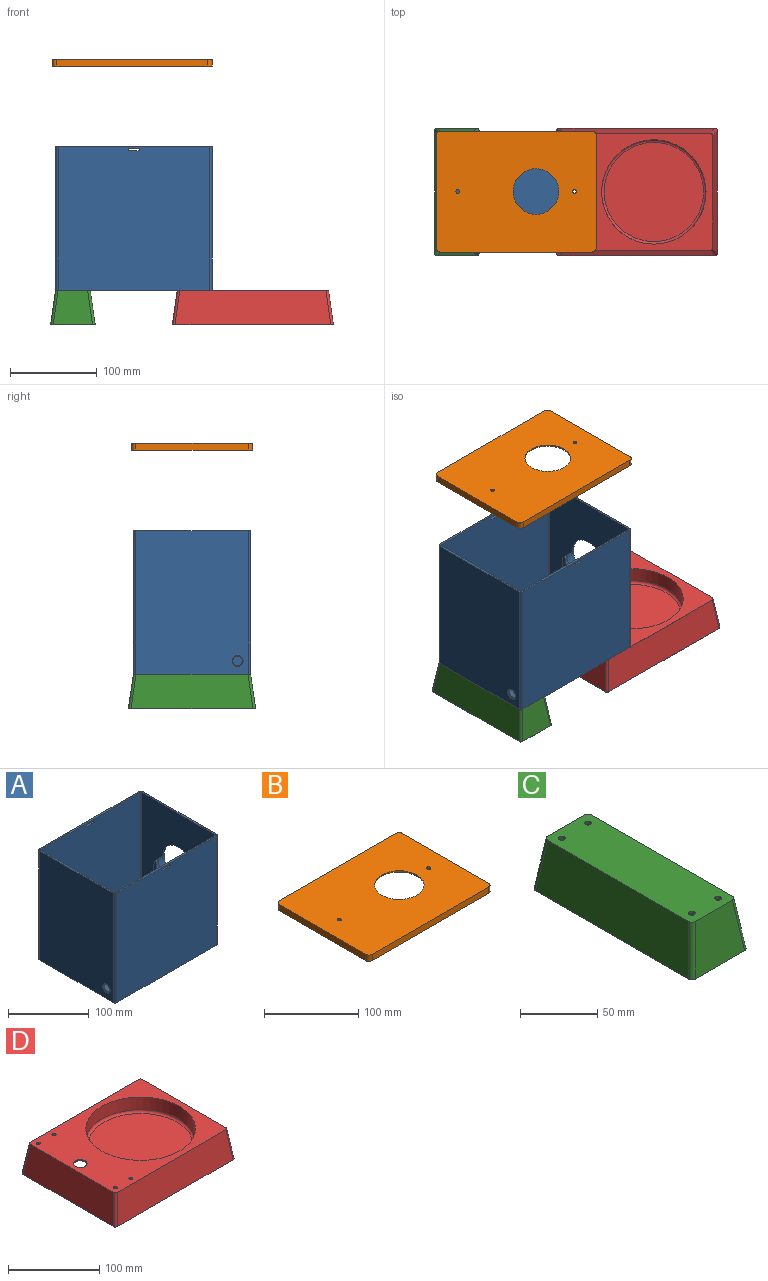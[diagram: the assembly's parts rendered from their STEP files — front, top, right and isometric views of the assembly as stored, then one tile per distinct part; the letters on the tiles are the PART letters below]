
ASSEMBLY  parts=4 mates=3
PART A: 56 faces, bbox 180x135x165 mm
  f0: plane 174x165mm, normal (0,-1,0), area 28678.7mm2, adj f6,f9,f10,f13,f41,f42,f43,f44
  f1: plane 174x162.8mm, normal (0,1,0), area 28295.9mm2, adj f4,f6,f16,f19,f41,f42,f43,f44
  f2: plane 174x165mm, normal (0,1,0), area 28678.7mm2, adj f6,f9,f11,f12,f37,f38,f39,f40
  f3: plane 174x162.8mm, normal (0,-1,0), area 28295.9mm2, adj f4,f6,f17,f18,f37,f38,f39,f40
  f4: plane 175.6x130.6mm, normal (0,0,1), area 21272.4mm2, adj f1,f3,f14,f15,f16,f17,f18,f19
  f5: plane 54x27mm, normal (1,0,0), area 277.6mm2, adj f20,f22,f23,f24
  f6: plane 180x135mm, normal (0,0,1), area 1359.5mm2, adj f0,f1,f2,f3,f7,f8,f10,f11
  f7: plane 165x129mm, normal (1,0,0), area 18994.8mm2, adj f6,f9,f10,f11,f20
  f8: plane 165x129mm, normal (-1,0,0), area 21160.3mm2, adj f6,f9,f12,f13,f36
  f9: plane 180x135mm, normal (0,0,-1), area 23954.2mm2, adj f0,f2,f7,f8,f10,f11,f12,f13
  f10: cylinder r=3mm len=165mm, axis (0,0,-1), area 777.5mm2, adj f0,f6,f7,f9
  f11: cylinder r=3mm len=165mm, axis (0,0,1), area 777.5mm2, adj f2,f6,f7,f9
  f12: cylinder r=3mm len=165mm, axis (0,0,-1), area 777.5mm2, adj f2,f6,f8,f9
  f13: cylinder r=3mm len=165mm, axis (0,0,1), area 777.5mm2, adj f0,f6,f8,f9
  f14: plane 162.8x129mm, normal (-1,0,0), area 14615.6mm2, adj f4,f6,f16,f17,f20,f21,f25
  f15: plane 162.8x129mm, normal (1,0,0), area 20876.5mm2, adj f4,f6,f18,f19,f35
  f16: cylinder r=0.8mm len=162.8mm, axis (0,0,-1), area 204.6mm2, adj f1,f4,f6,f14
  f17: cylinder r=0.8mm len=162.8mm, axis (0,0,1), area 204.6mm2, adj f3,f4,f6,f14
  f18: cylinder r=0.8mm len=162.8mm, axis (0,0,-1), area 204.6mm2, adj f3,f4,f6,f15
  f19: cylinder r=0.8mm len=162.8mm, axis (0,0,1), area 204.6mm2, adj f1,f4,f6,f15
  f20: cylinder r=27mm len=54mm, axis (1,0,0), area 1306.3mm2, adj f5,f7,f14,f21,f25
  f21: plane 84.8x15mm, normal (0,-1,0.09), area 1277.4mm2, adj f4,f14,f20,f22,f26
  f22: plane 4x3.5mm, normal (0,0,1), area 14mm2, adj f5,f21,f23,f26
  f23: cylinder r=23.5mm len=47mm, axis (1,0,0), area 295.3mm2, adj f5,f22,f24,f26
  f24: plane 4x3.5mm, normal (0,0,1), area 14mm2, adj f5,f23,f25,f26
  f25: plane 84.8x15mm, normal (0,1,0.09), area 1277.4mm2, adj f4,f14,f20,f24,f26
  f26: plane 84.8x69.6mm, normal (-1,0,0), area 4373mm2, adj f4,f21,f22,f23,f24,f25
  f27: cylinder r=23.5mm len=47mm, axis (-1,0,0), area 295.3mm2, adj f28,f31,f32,f33
  f28: plane 4x3.5mm, normal (0,0,1), area 14mm2, adj f27,f29,f32,f33
  f29: plane 84.8x7.8mm, normal (0,1,0.09), area 340.6mm2, adj f4,f28,f32,f33
  f30: plane 84.8x7.8mm, normal (0,-1,0.09), area 340.6mm2, adj f4,f31,f32,f33
  f31: plane 4x3.5mm, normal (0,0,1), area 14mm2, adj f27,f30,f32,f33
  f32: plane 84.8x69.6mm, normal (1,0,0), area 4373mm2, adj f4,f27,f28,f29,f30,f31
  f33: plane 84.8x69.6mm, normal (-1,0,0), area 4373mm2, adj f4,f27,f28,f29,f30,f31
  f34: cylinder r=5.5mm len=11mm, axis (-1,0,0), area 20.7mm2, adj f35,f36
  f35: torus R=6.3mm, axis (1,0,0), area 45.7mm2, adj f15,f34
  f36: torus R=6.3mm, axis (1,0,0), area 45.7mm2, adj f8,f34
  f37: plane 12.5x2.2mm, normal (0,0,1), area 27.5mm2, adj f2,f3,f38,f40
  f38: plane 2.5x2.2mm, normal (-1,0,0), area 5.5mm2, adj f2,f3,f37,f39
  f39: plane 12.5x2.2mm, normal (0,0,-1), area 27.5mm2, adj f2,f3,f38,f40
  f40: plane 2.5x2.2mm, normal (1,0,0), area 5.5mm2, adj f2,f3,f37,f39
  f41: plane 2.5x2.2mm, normal (1,0,0), area 5.5mm2, adj f0,f1,f42,f43
  f42: plane 12.5x2.2mm, normal (0,0,1), area 27.5mm2, adj f0,f1,f41,f44
  f43: plane 12.5x2.2mm, normal (0,0,-1), area 27.5mm2, adj f0,f1,f41,f44
  f44: plane 2.5x2.2mm, normal (-1,0,0), area 5.5mm2, adj f0,f1,f42,f43
  f45: cylinder r=7.5mm len=15mm, axis (0,0,-1), area 28.3mm2, adj f54,f55
  f46: cylinder r=2.2mm len=4.4mm, axis (0,0,-1), area 30.4mm2, adj f4,f9
  f47: cylinder r=2.2mm len=4.4mm, axis (0,0,-1), area 30.4mm2, adj f4,f9
  f48: cylinder r=2.2mm len=4.4mm, axis (0,0,-1), area 30.4mm2, adj f4,f9
  f49: cylinder r=2.2mm len=4.4mm, axis (0,0,-1), area 30.4mm2, adj f4,f9
  f50: cylinder r=2.2mm len=4.4mm, axis (0,0,-1), area 30.4mm2, adj f4,f9
  f51: cylinder r=2.2mm len=4.4mm, axis (0,0,-1), area 30.4mm2, adj f4,f9
  f52: cylinder r=2.2mm len=4.4mm, axis (0,0,-1), area 30.4mm2, adj f4,f9
  f53: cylinder r=2.2mm len=4.4mm, axis (0,0,-1), area 30.4mm2, adj f4,f9
  f54: torus R=8.3mm, axis (0,0,1), area 61.5mm2, adj f4,f45
  f55: torus R=8.3mm, axis (0,0,1), area 61.5mm2, adj f9,f45
PART B: 32 faces, bbox 184.2x139.2x8 mm
  f0: plane 184.2x139.2mm, normal (0,0,-1), area 1012.8mm2, adj f1,f2,f3,f4,f5,f6,f7,f8
  f1: plane 174x8mm, normal (0,-1,0), area 1392mm2, adj f0,f2,f8,f9
  f2: cylinder r=5.1mm len=8mm, axis (0,0,-1), area 64.1mm2, adj f0,f1,f3,f9
  f3: plane 129x8mm, normal (1,0,0), area 1032mm2, adj f0,f2,f4,f9
  f4: cylinder r=5.1mm len=8mm, axis (0,0,-1), area 64.1mm2, adj f0,f3,f5,f9
  f5: plane 174x8mm, normal (0,1,0), area 1392mm2, adj f0,f4,f6,f9
  f6: cylinder r=5.1mm len=8mm, axis (0,0,-1), area 64.1mm2, adj f0,f5,f7,f9
  f7: plane 129x8mm, normal (-1,0,0), area 1032mm2, adj f0,f6,f8,f9
  f8: cylinder r=5.1mm len=8mm, axis (0,0,-1), area 64.1mm2, adj f0,f1,f7,f9
  f9: plane 184.2x139.2mm, normal (0,0,1), area 23423.1mm2, adj f1,f2,f3,f4,f5,f6,f7,f8
  f10: plane 174x6.4mm, normal (0,1,0), area 1089.6mm2, adj f0,f11,f17,f18,f22,f23,f24,f25
  f11: cylinder r=3.5mm len=6.4mm, axis (0,0,-1), area 35.2mm2, adj f0,f10,f12,f18
  f12: plane 129x6.4mm, normal (-1,0,0), area 825.6mm2, adj f0,f11,f13,f18
  f13: cylinder r=3.5mm len=6.4mm, axis (0,0,-1), area 35.2mm2, adj f0,f12,f14,f18
  f14: plane 174x6.4mm, normal (0,-1,0), area 1089.6mm2, adj f0,f13,f15,f18,f27,f28,f29,f30
  f15: cylinder r=3.5mm len=6.4mm, axis (0,0,-1), area 35.2mm2, adj f0,f14,f16,f18
  f16: plane 129x6.4mm, normal (1,0,0), area 825.6mm2, adj f0,f15,f17,f18
  f17: cylinder r=3.5mm len=6.4mm, axis (0,0,-1), area 35.2mm2, adj f0,f10,f16,f18
  f18: plane 181x136mm, normal (0,0,-1), area 22410.3mm2, adj f10,f11,f12,f13,f14,f15,f16,f17
  f19: cylinder r=2.2mm len=4.4mm, axis (0,0,1), area 22.1mm2, adj f9,f18
  f20: cylinder r=2.2mm len=4.4mm, axis (0,0,1), area 22.1mm2, adj f9,f18
  f21: cylinder r=26.25mm len=52.5mm, axis (0,0,1), area 263.9mm2, adj f9,f18
  f22: plane 12x2mm, normal (0,0,-1), area 24mm2, adj f10,f23,f25,f26
  f23: plane 2x2mm, normal (-1,0,0), area 4mm2, adj f10,f22,f24,f26
  f24: plane 12x2mm, normal (0,0,1), area 24mm2, adj f10,f23,f25,f26
  f25: plane 2x2mm, normal (1,0,0), area 4mm2, adj f10,f22,f24,f26
  f26: plane 12x2mm, normal (0,1,0), area 24mm2, adj f22,f23,f24,f25
  f27: plane 12x2mm, normal (0,0,-1), area 24mm2, adj f14,f28,f30,f31
  f28: plane 2x2mm, normal (1,0,0), area 4mm2, adj f14,f27,f29,f31
  f29: plane 12x2mm, normal (0,0,1), area 24mm2, adj f14,f28,f30,f31
  f30: plane 2x2mm, normal (-1,0,0), area 4mm2, adj f14,f27,f29,f31
  f31: plane 12x2mm, normal (0,-1,0), area 24mm2, adj f27,f28,f29,f30
PART C: 23 faces, bbox 51.3x146.3x40.3 mm
  f0: plane 45.3x40mm, normal (0,-0.99,0.14), area 1602.8mm2, adj f4,f5,f6,f9
  f1: plane 140.3x40mm, normal (0.99,0,0.14), area 5440.1mm2, adj f4,f5,f6,f7
  f2: plane 45.3x40mm, normal (0,0.99,0.14), area 1602.8mm2, adj f4,f5,f7,f8
  f3: plane 140.3x40mm, normal (-0.99,0,0.14), area 5440.1mm2, adj f4,f5,f8,f9
  f4: plane 146.24x51.24mm, normal (0,0,-1), area 615.7mm2, adj f0,f1,f2,f3,f6,f7,f8,f9
  f5: plane 135x40mm, normal (0,0,1), area 5331.7mm2, adj f0,f1,f2,f3,f6,f7,f8,f9
  f6: cylinder r=3mm len=40.34mm, axis (-0.14,0.14,0.98), area 189.8mm2, adj f0,f1,f4,f5
  f7: cylinder r=3mm len=40.34mm, axis (-0.14,-0.14,0.98), area 189.8mm2, adj f1,f2,f4,f5
  f8: cylinder r=3mm len=40.34mm, axis (0.14,-0.14,0.98), area 189.8mm2, adj f2,f3,f4,f5
  f9: cylinder r=3mm len=40.34mm, axis (0.14,0.14,0.98), area 189.8mm2, adj f0,f3,f4,f5
  f10: plane 45.24x38.42mm, normal (0,0.99,-0.14), area 1545.6mm2, adj f4,f14,f15,f18
  f11: plane 140.24x38.42mm, normal (-0.99,0,-0.14), area 5230.9mm2, adj f4,f14,f15,f16
  f12: plane 45.24x38.42mm, normal (0,-0.99,-0.14), area 1545.6mm2, adj f4,f14,f16,f17
  f13: plane 140.24x38.42mm, normal (0.99,0,-0.14), area 5230.9mm2, adj f4,f14,f17,f18
  f14: plane 132.25x37.25mm, normal (0,0,-1), area 4863.2mm2, adj f10,f11,f12,f13,f15,f16,f17,f18
  f15: cylinder r=1.42mm len=38.57mm, axis (-0.14,0.14,0.98), area 86mm2, adj f4,f10,f11,f14
  f16: cylinder r=1.42mm len=38.57mm, axis (-0.14,-0.14,0.98), area 86mm2, adj f4,f11,f12,f14
  f17: cylinder r=1.42mm len=38.57mm, axis (0.14,-0.14,0.98), area 86mm2, adj f4,f12,f13,f14
  f18: cylinder r=1.42mm len=38.57mm, axis (0.14,0.14,0.98), area 86mm2, adj f4,f10,f13,f14
  f19: cylinder r=2.2mm len=4.4mm, axis (0,0,1), area 21.9mm2, adj f5,f14
  f20: cylinder r=2.2mm len=4.4mm, axis (0,0,1), area 21.9mm2, adj f5,f14
  f21: cylinder r=2.2mm len=4.4mm, axis (0,0,1), area 21.9mm2, adj f5,f14
  f22: cylinder r=2.2mm len=4.4mm, axis (0,0,1), area 21.9mm2, adj f5,f14
PART D: 54 faces, bbox 185.3x146.3x40.3 mm
  f0: plane 185.24x146.24mm, normal (0,0,-1), area 1099.7mm2, adj f3,f4,f5,f6,f10,f11,f12,f13
  f1: plane 142.9x37.9mm, normal (-0.99,0,-0.14), area 5132.6mm2, adj f3,f5,f7,f9,f42,f43,f44,f45
  f2: plane 142.85x37.73mm, normal (0.99,0,0.14), area 5159mm2, adj f4,f6,f8,f35,f36,f37,f38,f39
  f3: plane 176.01x38.42mm, normal (0,0.99,-0.14), area 6598.6mm2, adj f0,f1,f7,f29,f48
  f4: plane 38.42x7.53mm, normal (0,0.99,-0.14), area 82.8mm2, adj f0,f2,f8,f26,f35
  f5: plane 176.01x38.42mm, normal (0,-0.99,-0.14), area 6598.6mm2, adj f0,f1,f7,f28,f42
  f6: plane 38.42x7.53mm, normal (0,-0.99,-0.14), area 82.8mm2, adj f0,f2,f8,f27,f41
  f7: plane 166.1x132.25mm, normal (0,0,-1), area 9819.5mm2, adj f1,f3,f5,f9,f23,f28,f29,f49
  f8: plane 132.25x3.53mm, normal (0,0,-1), area 466.6mm2, adj f2,f4,f6,f22,f26,f27
  f9: cylinder r=61.58mm len=123.17mm, axis (0,0,1), area 5914.8mm2, adj f1,f7,f25
  f10: plane 179.3x40mm, normal (0,-0.99,0.14), area 7015.5mm2, adj f0,f14,f18,f21
  f11: plane 140.3x40mm, normal (0.99,0,0.14), area 5440.1mm2, adj f0,f14,f18,f19
  f12: plane 179.3x40mm, normal (0,0.99,0.14), area 7015.5mm2, adj f0,f14,f19,f20
  f13: plane 140.3x40mm, normal (-0.99,0,0.14), area 5440.1mm2, adj f0,f14,f20,f21
  f14: plane 174x135mm, normal (0,0,1), area 11935.2mm2, adj f10,f11,f12,f13,f15,f18,f19,f20
  f15: cylinder r=60mm len=120mm, axis (0,0,1), area 6408.8mm2, adj f14,f17
  f16: plane 114x114mm, normal (0,0,1), area 10207mm2, adj f17
  f17: torus R=57mm, axis (0,0,1), area 1744.3mm2, adj f15,f16
  f18: cylinder r=3mm len=40.34mm, axis (-0.14,0.14,0.98), area 189.8mm2, adj f0,f10,f11,f14
  f19: cylinder r=3mm len=40.34mm, axis (-0.14,-0.14,0.98), area 189.8mm2, adj f0,f11,f12,f14
  f20: cylinder r=3mm len=40.34mm, axis (0.14,-0.14,0.98), area 189.8mm2, adj f0,f12,f13,f14
  f21: cylinder r=3mm len=40.34mm, axis (0.14,0.14,0.98), area 189.8mm2, adj f0,f10,f13,f14
  f22: plane 140.24x38.42mm, normal (-0.99,0,-0.14), area 5230.9mm2, adj f0,f8,f26,f27
  f23: plane 140.24x38.42mm, normal (0.99,0,-0.14), area 5230.9mm2, adj f0,f7,f28,f29
  f24: plane 114x114mm, normal (0,0,-1), area 10207mm2, adj f25
  f25: torus R=57mm, axis (0,0,1), area 2710.8mm2, adj f9,f24
  f26: cylinder r=1.42mm len=38.57mm, axis (-0.14,0.14,0.98), area 86mm2, adj f0,f4,f8,f22
  f27: cylinder r=1.42mm len=38.57mm, axis (-0.14,-0.14,0.98), area 86mm2, adj f0,f6,f8,f22
  f28: cylinder r=1.42mm len=38.57mm, axis (0.14,-0.14,0.98), area 86mm2, adj f0,f5,f7,f23
  f29: cylinder r=1.42mm len=38.57mm, axis (0.14,0.14,0.98), area 86mm2, adj f0,f3,f7,f23
  f30: plane 16.74x2.75mm, normal (0,-1,0), area 6.7mm2, adj f32,f33,f39,f44
  f31: plane 16.74x2.75mm, normal (0,1,0), area 6.7mm2, adj f33,f34,f37,f46
  f32: cylinder r=1.5mm len=1.5mm, axis (1,0,0), area 1mm2, adj f0,f30,f40,f43
  f33: cylinder r=1.5mm len=3mm, axis (-0.99,0,-0.14), area 1.9mm2, adj f30,f31,f38,f45
  f34: cylinder r=1.5mm len=1.5mm, axis (-1,0,0), area 1mm2, adj f0,f31,f36,f47
  f35: cylinder r=0.6mm len=68.52mm, axis (0,-1,0), area 70.3mm2, adj f0,f2,f4,f36
  f36: bspline ~1.65x1.57mm, area 2mm2, adj f2,f34,f35,f37
  f37: cylinder r=0.6mm len=16.82mm, axis (0.14,0,-0.99), area 15.9mm2, adj f2,f31,f36,f38
  f38: torus R=2.1mm, axis (-0.99,0,-0.14), area 5.1mm2, adj f2,f33,f37,f39
  f39: cylinder r=0.6mm len=16.82mm, axis (-0.14,0,0.99), area 15.9mm2, adj f2,f30,f38,f40
  f40: bspline ~1.65x1.5mm, area 2mm2, adj f2,f32,f39,f41
  f41: cylinder r=0.6mm len=68.52mm, axis (0,-1,0), area 70.3mm2, adj f0,f2,f6,f40
  f42: cylinder r=0.6mm len=68.52mm, axis (0,-1,0), area 58.8mm2, adj f0,f1,f5,f43
  f43: bspline ~1.76x1.5mm, area 1.8mm2, adj f1,f32,f42,f44
  f44: cylinder r=0.6mm len=16.76mm, axis (0.14,0,-0.99), area 15.9mm2, adj f1,f30,f43,f45
  f45: torus R=2.1mm, axis (0.99,0,0.14), area 5.1mm2, adj f1,f33,f44,f46
  f46: cylinder r=0.6mm len=16.76mm, axis (-0.14,0,0.99), area 15.9mm2, adj f1,f31,f45,f47
  f47: bspline ~1.76x1.76mm, area 1.8mm2, adj f1,f34,f46,f48
  f48: cylinder r=0.6mm len=68.52mm, axis (0,-1,0), area 58.8mm2, adj f0,f1,f3,f47
  f49: cylinder r=2.2mm len=4.4mm, axis (0,0,1), area 21.9mm2, adj f7,f14
  f50: cylinder r=2.2mm len=4.4mm, axis (0,0,1), area 21.9mm2, adj f7,f14
  f51: cylinder r=2.2mm len=4.4mm, axis (0,0,1), area 21.9mm2, adj f7,f14
  f52: cylinder r=2.2mm len=4.4mm, axis (0,0,1), area 21.9mm2, adj f7,f14
  f53: cylinder r=7.5mm len=15mm, axis (0,0,1), area 74.6mm2, adj f7,f14
PLACE A t=(8.23,-0.31,148.78)mm
PLACE B t=(6.44,-0.31,216.43)mm
PLACE C t=(-61.77,-0.31,148.78)mm
PLACE D t=(145.23,-0.31,148.78)mm
MATE fastened D.f49 <-> A.f49  axis (0,0,1) through (66.23,59.19,148.78)mm
MATE fastened C.f19 <-> A.f51  axis (0,0,1) through (-73.77,59.19,148.78)mm
MATE slider B.f18 <-> A.f6  axis (0,0,-1) through (4.23,-0.31,412.83)mm
